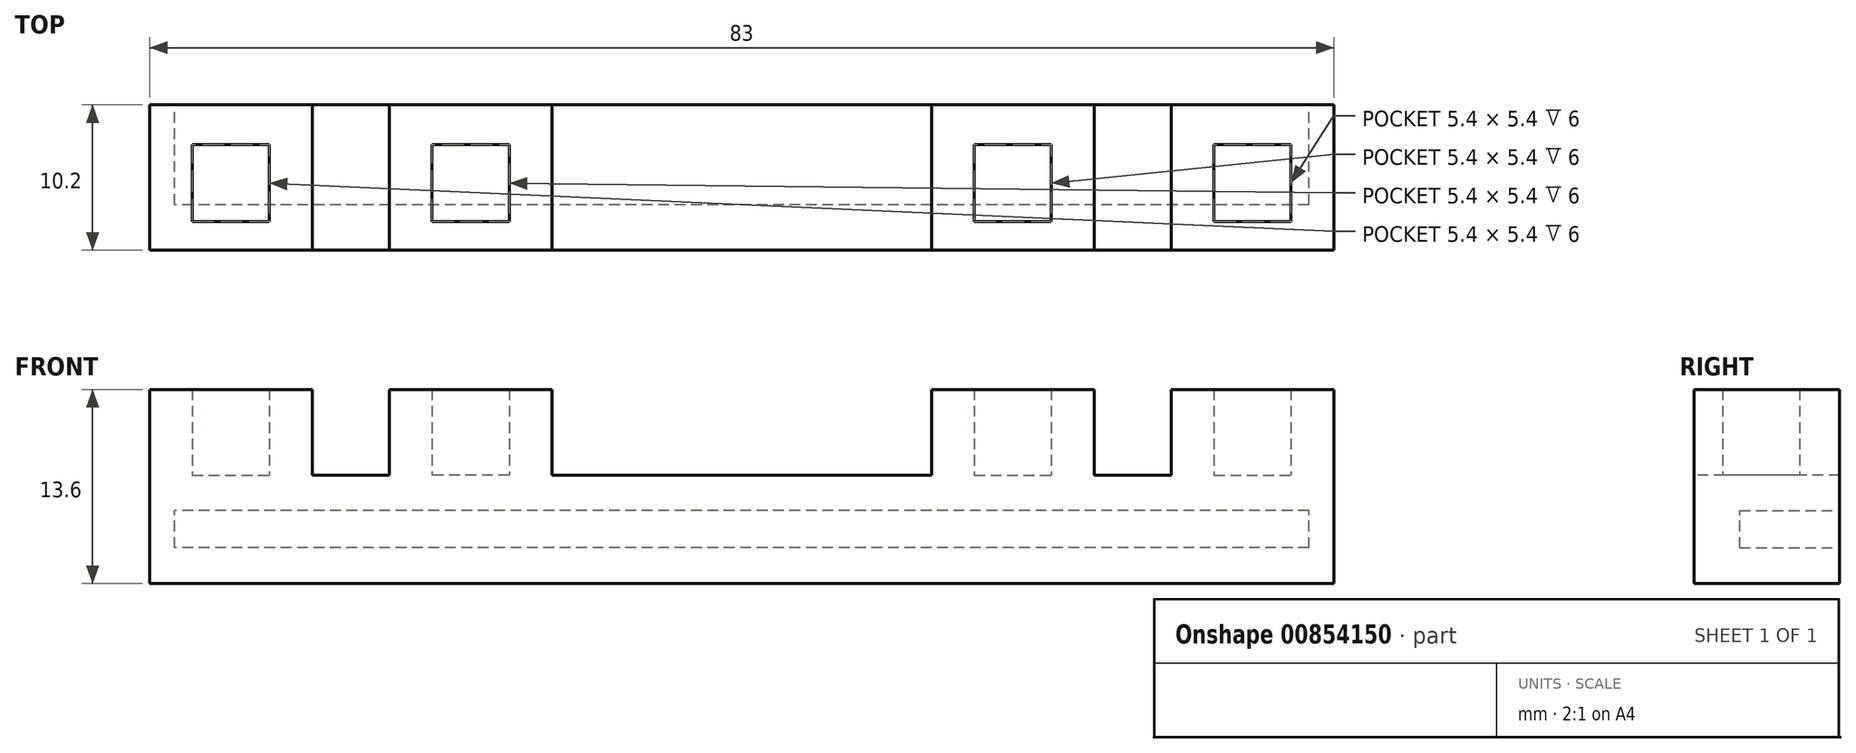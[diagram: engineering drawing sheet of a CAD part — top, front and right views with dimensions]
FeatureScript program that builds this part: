
annotation { "Feature Type Name" : "Feature", "Feature Type Description" : "" }
export const myFeature = defineFeature(function(context is Context, id is Id, definition is map)
    precondition{}
    {
        {
            var Q0;
            Q0=qCreatedBy(makeId("Front.planeOp"),FACE);
            var sketch = newSketch(context, id + "F0", { "sketchPlane" : qUnion([Q0])});
            skLineSegment(sketch, "E0.bottom", {"start": v(41.5, -3.8) * mm, "end": v(-41.5, -3.8) * mm});
            skLineSegment(sketch, "E0.top", {"start": v(41.5, 3.8) * mm, "end": v(-41.5, 3.8) * mm});
            skLineSegment(sketch, "E0.left", {"start": v(41.5, -3.8) * mm, "end": v(41.5, 3.8) * mm});
            skLineSegment(sketch, "E0.right", {"start": v(-41.5, -3.8) * mm, "end": v(-41.5, 3.8) * mm});
            skPoint(sketch, "E0.middle", {"position": v(0, 0) * mm});
            skLineSegment(sketch, "E1.bottom", {"start": v(39.75, -1.3) * mm, "end": v(-39.75, -1.3) * mm});
            skLineSegment(sketch, "E1.top", {"start": v(39.75, 1.3) * mm, "end": v(-39.75, 1.3) * mm});
            skLineSegment(sketch, "E1.left", {"start": v(39.75, -1.3) * mm, "end": v(39.75, 1.3) * mm});
            skLineSegment(sketch, "E1.right", {"start": v(-39.75, -1.3) * mm, "end": v(-39.75, 1.3) * mm});
            skSolve(sketch);
        }
        {
            var Q0;
            Q0=makeQuery(id+"F0.imprint","IMPRINT",FACE,{"disambiguationData":[TD([[makeQuery(id+"F0.imprint","IMPRINT",EDGE,{"derivedFrom":sQuery(id+"F0.wireOp",EDGE,"E0.bottom")}),-1.0]])]});
            extrude(context, id + "F1", {"entities" : qUnion([Q0]), "depth" : 7 * mm, "offsetDistance" : 25 * mm});
        }
        {
            var Q0;
            Q0=makeQuery(id+"F1.opExtrude","CAP_FACE",FACE,{"disambiguationData":[OSD([sQuery(id+"F0.wireOp",EDGE,"E0.bottom"),sQuery(id+"F0.wireOp",EDGE,"E0.top"),sQuery(id+"F0.wireOp",EDGE,"E0.left"),sQuery(id+"F0.wireOp",EDGE,"E0.right"),sQuery(id+"F0.wireOp",EDGE,"E1.bottom"),sQuery(id+"F0.wireOp",EDGE,"E1.top"),sQuery(id+"F0.wireOp",EDGE,"E1.left"),sQuery(id+"F0.wireOp",EDGE,"E1.right")])],"isStart":false});
            var sketch = newSketch(context, id + "F2", { "sketchPlane" : qUnion([Q0])});
            skLineSegment(sketch, "E2.bottom", {"start": v(-41.5, 3.8) * mm, "end": v(41.5, 3.8) * mm});
            skLineSegment(sketch, "E2.top", {"start": v(-41.5, -3.8) * mm, "end": v(41.5, -3.8) * mm});
            skLineSegment(sketch, "E2.left", {"start": v(-41.5, 3.8) * mm, "end": v(-41.5, -3.8) * mm});
            skLineSegment(sketch, "E2.right", {"start": v(41.5, 3.8) * mm, "end": v(41.5, -3.8) * mm});
            skSolve(sketch);
        }
        {
            var Q0;
            Q0=makeQuery(id+"F2.imprint","IMPRINT",FACE,{"disambiguationData":[TD([[makeQuery(id+"F2.imprint","IMPRINT",EDGE,{"derivedFrom":sQuery(id+"F2.wireOp",EDGE,"E2.bottom")}),1.0]])]});
            var Q1;
            Q1=makeQuery(id+"F2.imprint","IMPRINT",FACE,{"disambiguationData":[TD([[makeQuery(id+"F2.imprint","IMPRINT",EDGE,{"derivedFrom":makeQuery(id+"F1.opExtrude","CAP_EDGE",EDGE,{"disambiguationData":[OSD([sQuery(id+"F0.wireOp",EDGE,"E1.bottom")])],"isStart":false})}),-1.0]])]});
            extrude(context, id + "F3", {"entities" : qUnion([Q0, Q1]), "operationType" : NewBodyOperationType.ADD, "depth" : 3.2 * mm, "offsetDistance" : 25 * mm});
        }
        {
            var Q0;
            Q0=makeQuery(id+"F3.boolean.opBoolean","MERGE",FACE,{"derivedFrom":[makeQuery(id+"F1.opExtrude","SWEPT_FACE",FACE,{"disambiguationData":[OSD([sQuery(id+"F0.wireOp",EDGE,"E0.top")])]}),makeQuery(id+"F3.opExtrude","SWEPT_FACE",FACE,{"disambiguationData":[OSD([sQuery(id+"F2.wireOp",EDGE,"E2.bottom")])]})]});
            var sketch = newSketch(context, id + "F4", { "sketchPlane" : qUnion([Q0])});
            skLineSegment(sketch, "E3.bottom", {"start": v(-41.5, -10.2) * mm, "end": v(41.5, -10.2) * mm});
            skLineSegment(sketch, "E3.top", {"start": v(-41.5, 0) * mm, "end": v(41.5, 0) * mm});
            skLineSegment(sketch, "E3.left", {"start": v(-41.5, -10.2) * mm, "end": v(-41.5, 0) * mm});
            skLineSegment(sketch, "E4", {"start": v(0.5, 0) * mm, "end": v(0.5, -10.2) * mm});
            skLineSegment(sketch, "E5", {"start": v(-4.9, 0) * mm, "end": v(-4.9, -10.2) * mm});
            skLineSegment(sketch, "E6", {"start": v(-7.9, 0) * mm, "end": v(-7.9, -10.2) * mm});
            skLineSegment(sketch, "E7", {"start": v(-13.3, 0) * mm, "end": v(-13.3, -10.2) * mm});
            skLineSegment(sketch, "E8", {"start": v(-16.3, 0) * mm, "end": v(-16.3, -10.2) * mm});
            skLineSegment(sketch, "E9", {"start": v(-21.7, 0) * mm, "end": v(-21.7, -10.2) * mm});
            skLineSegment(sketch, "E10", {"start": v(-24.7, 0) * mm, "end": v(-24.7, -10.2) * mm});
            skLineSegment(sketch, "E11", {"start": v(-30.1, 0) * mm, "end": v(-30.1, -10.2) * mm});
            skLineSegment(sketch, "E12", {"start": v(-33.1, 0) * mm, "end": v(-33.1, -10.2) * mm});
            skLineSegment(sketch, "E13", {"start": v(-38.5, 0) * mm, "end": v(-38.5, -10.2) * mm});
            skLineSegment(sketch, "E14", {"start": v(0, 0) * mm, "end": v(0, -13.13) * mm, "construction": true});
            skLineSegment(sketch, "E15.MirrorCS", {"start": v(-0.5, 0) * mm, "end": v(-0.5, -10.2) * mm});
            skLineSegment(sketch, "E16", {"start": v(-41.5, -2.8) * mm, "end": v(41.5, -2.8) * mm});
            skLineSegment(sketch, "E17", {"start": v(41.5, -8.2) * mm, "end": v(-41.5, -8.2) * mm});
            skLineSegment(sketch, "E18.MirrorCS", {"start": v(16.3, 0) * mm, "end": v(16.3, -10.2) * mm});
            skLineSegment(sketch, "E19.MirrorCS", {"start": v(21.7, 0) * mm, "end": v(21.7, -10.2) * mm});
            skLineSegment(sketch, "E20.MirrorCS", {"start": v(24.7, 0) * mm, "end": v(24.7, -10.2) * mm});
            skLineSegment(sketch, "E21.MirrorCS", {"start": v(30.1, 0) * mm, "end": v(30.1, -10.2) * mm});
            skLineSegment(sketch, "E22.MirrorCS", {"start": v(33.1, 0) * mm, "end": v(33.1, -10.2) * mm});
            skLineSegment(sketch, "E23.MirrorCS", {"start": v(38.5, 0) * mm, "end": v(38.5, -10.2) * mm});
            skLineSegment(sketch, "E24.MirrorCS", {"start": v(41.5, -10.2) * mm, "end": v(41.5, 0) * mm});
            skLineSegment(sketch, "E25.MirrorCS", {"start": v(4.9, 0) * mm, "end": v(4.9, -10.2) * mm});
            skLineSegment(sketch, "E26.MirrorCS", {"start": v(13.3, 0) * mm, "end": v(13.3, -10.2) * mm});
            skLineSegment(sketch, "E27.MirrorCS", {"start": v(7.9, 0) * mm, "end": v(7.9, -10.2) * mm});
            skSolve(sketch);
        }
        {
            var Q0;
            {var subQ1=sQuery(id+"F4.wireOp",EDGE,"E3.top");var subQ3=sQuery(id+"F4.wireOp",EDGE,"E13");var subQ4=makeQuery(id+"F4.imprint","INTERSECT",VERTEX,{"derivedFrom":[subQ1,subQ3]});Q0=makeQuery(id+"F4.imprint","IMPRINT",FACE,{"disambiguationData":[TD([[makeQuery(id+"F4.imprint","IMPRINT",EDGE,{"disambiguationData":[TD([[subQ4,-1.0]])],"derivedFrom":subQ3}),-1.0]])]});}
            var Q1;
            {var subQ0=sQuery(id+"F4.wireOp",EDGE,"E12");var subQ1=sQuery(id+"F4.wireOp",EDGE,"E3.top");var subQ2=makeQuery(id+"F4.imprint","INTERSECT",VERTEX,{"derivedFrom":[subQ1,subQ0]});Q1=makeQuery(id+"F4.imprint","IMPRINT",FACE,{"disambiguationData":[TD([[makeQuery(id+"F4.imprint","IMPRINT",EDGE,{"disambiguationData":[TD([[subQ2,1.0]])],"derivedFrom":subQ1}),-1.0]])]});}
            var Q2;
            {var subQ0=sQuery(id+"F4.wireOp",EDGE,"E11");var subQ1=sQuery(id+"F4.wireOp",EDGE,"E3.top");var subQ2=makeQuery(id+"F4.imprint","INTERSECT",VERTEX,{"derivedFrom":[subQ1,subQ0]});Q2=makeQuery(id+"F4.imprint","IMPRINT",FACE,{"disambiguationData":[TD([[makeQuery(id+"F4.imprint","IMPRINT",EDGE,{"disambiguationData":[TD([[subQ2,1.0]])],"derivedFrom":subQ1}),-1.0]])]});}
            var Q3;
            {var subQ0=sQuery(id+"F4.wireOp",EDGE,"E9");var subQ1=sQuery(id+"F4.wireOp",EDGE,"E3.top");var subQ2=makeQuery(id+"F4.imprint","INTERSECT",VERTEX,{"derivedFrom":[subQ1,subQ0]});Q3=makeQuery(id+"F4.imprint","IMPRINT",FACE,{"disambiguationData":[TD([[makeQuery(id+"F4.imprint","IMPRINT",EDGE,{"disambiguationData":[TD([[subQ2,1.0]])],"derivedFrom":subQ1}),-1.0]])]});}
            var Q4;
            {var subQ0=sQuery(id+"F4.wireOp",EDGE,"E8");var subQ1=sQuery(id+"F4.wireOp",EDGE,"E3.top");var subQ2=makeQuery(id+"F4.imprint","INTERSECT",VERTEX,{"derivedFrom":[subQ1,subQ0]});Q4=makeQuery(id+"F4.imprint","IMPRINT",FACE,{"disambiguationData":[TD([[makeQuery(id+"F4.imprint","IMPRINT",EDGE,{"disambiguationData":[TD([[subQ2,1.0]])],"derivedFrom":subQ1}),-1.0]])]});}
            var Q5;
            {var subQ0=sQuery(id+"F4.wireOp",EDGE,"E7");var subQ1=sQuery(id+"F4.wireOp",EDGE,"E3.top");var subQ2=makeQuery(id+"F4.imprint","INTERSECT",VERTEX,{"derivedFrom":[subQ1,subQ0]});Q5=makeQuery(id+"F4.imprint","IMPRINT",FACE,{"disambiguationData":[TD([[makeQuery(id+"F4.imprint","IMPRINT",EDGE,{"disambiguationData":[TD([[subQ2,1.0]])],"derivedFrom":subQ1}),-1.0]])]});}
            var Q6;
            {var subQ0=sQuery(id+"F4.wireOp",EDGE,"E18.MirrorCS");var subQ1=sQuery(id+"F4.wireOp",EDGE,"E3.top");var subQ2=makeQuery(id+"F4.imprint","INTERSECT",VERTEX,{"derivedFrom":[subQ1,subQ0]});Q6=makeQuery(id+"F4.imprint","IMPRINT",FACE,{"disambiguationData":[TD([[makeQuery(id+"F4.imprint","IMPRINT",EDGE,{"disambiguationData":[TD([[subQ2,1.0]])],"derivedFrom":subQ1}),-1.0]])]});}
            var Q7;
            {var subQ0=sQuery(id+"F4.wireOp",EDGE,"E18.MirrorCS");var subQ1=sQuery(id+"F4.wireOp",EDGE,"E3.top");var subQ2=makeQuery(id+"F4.imprint","INTERSECT",VERTEX,{"derivedFrom":[subQ1,subQ0]});Q7=makeQuery(id+"F4.imprint","IMPRINT",FACE,{"disambiguationData":[TD([[makeQuery(id+"F4.imprint","IMPRINT",EDGE,{"disambiguationData":[TD([[subQ2,-1.0]])],"derivedFrom":subQ1}),-1.0]])]});}
            var Q8;
            {var subQ0=sQuery(id+"F4.wireOp",EDGE,"E19.MirrorCS");var subQ1=sQuery(id+"F4.wireOp",EDGE,"E3.top");var subQ2=makeQuery(id+"F4.imprint","INTERSECT",VERTEX,{"derivedFrom":[subQ1,subQ0]});Q8=makeQuery(id+"F4.imprint","IMPRINT",FACE,{"disambiguationData":[TD([[makeQuery(id+"F4.imprint","IMPRINT",EDGE,{"disambiguationData":[TD([[subQ2,-1.0]])],"derivedFrom":subQ1}),-1.0]])]});}
            var Q9;
            {var subQ0=sQuery(id+"F4.wireOp",EDGE,"E21.MirrorCS");var subQ1=sQuery(id+"F4.wireOp",EDGE,"E3.top");var subQ2=makeQuery(id+"F4.imprint","INTERSECT",VERTEX,{"derivedFrom":[subQ1,subQ0]});Q9=makeQuery(id+"F4.imprint","IMPRINT",FACE,{"disambiguationData":[TD([[makeQuery(id+"F4.imprint","IMPRINT",EDGE,{"disambiguationData":[TD([[subQ2,-1.0]])],"derivedFrom":subQ1}),-1.0]])]});}
            var Q10;
            {var subQ0=sQuery(id+"F4.wireOp",EDGE,"E22.MirrorCS");var subQ1=sQuery(id+"F4.wireOp",EDGE,"E3.top");var subQ2=makeQuery(id+"F4.imprint","INTERSECT",VERTEX,{"derivedFrom":[subQ1,subQ0]});Q10=makeQuery(id+"F4.imprint","IMPRINT",FACE,{"disambiguationData":[TD([[makeQuery(id+"F4.imprint","IMPRINT",EDGE,{"disambiguationData":[TD([[subQ2,-1.0]])],"derivedFrom":subQ1}),-1.0]])]});}
            var Q11;
            {var subQ0=sQuery(id+"F4.wireOp",EDGE,"E24.MirrorCS");var subQ5=sQuery(id+"F4.wireOp",EDGE,"E16");var subQ6=makeQuery(id+"F4.imprint","INTERSECT",VERTEX,{"derivedFrom":[subQ5,subQ0]});Q11=makeQuery(id+"F4.imprint","IMPRINT",FACE,{"disambiguationData":[TD([[makeQuery(id+"F4.imprint","IMPRINT",EDGE,{"disambiguationData":[TD([[subQ6,1.0]])],"derivedFrom":subQ5}),1.0]])]});}
            var Q12;
            {var subQ0=sQuery(id+"F4.wireOp",EDGE,"E16");var subQ1=sQuery(id+"F4.wireOp",EDGE,"E3.left");var subQ2=makeQuery(id+"F4.imprint","INTERSECT",VERTEX,{"derivedFrom":[subQ1,subQ0]});Q12=makeQuery(id+"F4.imprint","IMPRINT",FACE,{"disambiguationData":[TD([[makeQuery(id+"F4.imprint","IMPRINT",EDGE,{"disambiguationData":[TD([[subQ2,1.0]])],"derivedFrom":subQ1}),-1.0]])]});}
            var Q13;
            {var subQ0=sQuery(id+"F4.wireOp",EDGE,"E3.left");var subQ1=sQuery(id+"F4.wireOp",EDGE,"E3.bottom");var subQ2=makeQuery(id+"F4.imprint","INTERSECT",VERTEX,{"derivedFrom":[subQ1,subQ0]});Q13=makeQuery(id+"F4.imprint","IMPRINT",FACE,{"disambiguationData":[TD([[makeQuery(id+"F4.imprint","IMPRINT",EDGE,{"disambiguationData":[TD([[subQ2,1.0]])],"derivedFrom":subQ1}),-1.0]])]});}
            var Q14;
            {var subQ0=sQuery(id+"F4.wireOp",EDGE,"E12");var subQ1=sQuery(id+"F4.wireOp",EDGE,"E3.bottom");var subQ2=makeQuery(id+"F4.imprint","INTERSECT",VERTEX,{"derivedFrom":[subQ1,subQ0]});Q14=makeQuery(id+"F4.imprint","IMPRINT",FACE,{"disambiguationData":[TD([[makeQuery(id+"F4.imprint","IMPRINT",EDGE,{"disambiguationData":[TD([[subQ2,-1.0]])],"derivedFrom":subQ1}),-1.0]])]});}
            var Q15;
            {var subQ0=sQuery(id+"F4.wireOp",EDGE,"E11");var subQ1=sQuery(id+"F4.wireOp",EDGE,"E3.bottom");var subQ2=makeQuery(id+"F4.imprint","INTERSECT",VERTEX,{"derivedFrom":[subQ1,subQ0]});Q15=makeQuery(id+"F4.imprint","IMPRINT",FACE,{"disambiguationData":[TD([[makeQuery(id+"F4.imprint","IMPRINT",EDGE,{"disambiguationData":[TD([[subQ2,-1.0]])],"derivedFrom":subQ1}),-1.0]])]});}
            var Q16;
            {var subQ0=sQuery(id+"F4.wireOp",EDGE,"E16");var subQ1=sQuery(id+"F4.wireOp",EDGE,"E11");var subQ2=makeQuery(id+"F4.imprint","INTERSECT",VERTEX,{"derivedFrom":[subQ1,subQ0]});Q16=makeQuery(id+"F4.imprint","IMPRINT",FACE,{"disambiguationData":[TD([[makeQuery(id+"F4.imprint","IMPRINT",EDGE,{"disambiguationData":[TD([[subQ2,-1.0]])],"derivedFrom":subQ1}),-1.0]])]});}
            var Q17;
            {var subQ0=sQuery(id+"F4.wireOp",EDGE,"E9");var subQ1=sQuery(id+"F4.wireOp",EDGE,"E3.bottom");var subQ2=makeQuery(id+"F4.imprint","INTERSECT",VERTEX,{"derivedFrom":[subQ1,subQ0]});Q17=makeQuery(id+"F4.imprint","IMPRINT",FACE,{"disambiguationData":[TD([[makeQuery(id+"F4.imprint","IMPRINT",EDGE,{"disambiguationData":[TD([[subQ2,-1.0]])],"derivedFrom":subQ1}),-1.0]])]});}
            var Q18;
            {var subQ0=sQuery(id+"F4.wireOp",EDGE,"E8");var subQ1=sQuery(id+"F4.wireOp",EDGE,"E3.bottom");var subQ2=makeQuery(id+"F4.imprint","INTERSECT",VERTEX,{"derivedFrom":[subQ1,subQ0]});Q18=makeQuery(id+"F4.imprint","IMPRINT",FACE,{"disambiguationData":[TD([[makeQuery(id+"F4.imprint","IMPRINT",EDGE,{"disambiguationData":[TD([[subQ2,-1.0]])],"derivedFrom":subQ1}),-1.0]])]});}
            var Q19;
            {var subQ0=sQuery(id+"F4.wireOp",EDGE,"E16");var subQ1=sQuery(id+"F4.wireOp",EDGE,"E9");var subQ2=makeQuery(id+"F4.imprint","INTERSECT",VERTEX,{"derivedFrom":[subQ1,subQ0]});Q19=makeQuery(id+"F4.imprint","IMPRINT",FACE,{"disambiguationData":[TD([[makeQuery(id+"F4.imprint","IMPRINT",EDGE,{"disambiguationData":[TD([[subQ2,-1.0]])],"derivedFrom":subQ1}),-1.0]])]});}
            var Q20;
            {var subQ0=sQuery(id+"F4.wireOp",EDGE,"E16");var subQ1=sQuery(id+"F4.wireOp",EDGE,"E7");var subQ2=makeQuery(id+"F4.imprint","INTERSECT",VERTEX,{"derivedFrom":[subQ1,subQ0]});Q20=makeQuery(id+"F4.imprint","IMPRINT",FACE,{"disambiguationData":[TD([[makeQuery(id+"F4.imprint","IMPRINT",EDGE,{"disambiguationData":[TD([[subQ2,-1.0]])],"derivedFrom":subQ1}),-1.0]])]});}
            var Q21;
            {var subQ0=sQuery(id+"F4.wireOp",EDGE,"E7");var subQ1=sQuery(id+"F4.wireOp",EDGE,"E3.bottom");var subQ2=makeQuery(id+"F4.imprint","INTERSECT",VERTEX,{"derivedFrom":[subQ1,subQ0]});Q21=makeQuery(id+"F4.imprint","IMPRINT",FACE,{"disambiguationData":[TD([[makeQuery(id+"F4.imprint","IMPRINT",EDGE,{"disambiguationData":[TD([[subQ2,-1.0]])],"derivedFrom":subQ1}),-1.0]])]});}
            var Q22;
            {var subQ0=sQuery(id+"F4.wireOp",EDGE,"E24.MirrorCS");var subQ1=sQuery(id+"F4.wireOp",EDGE,"E3.bottom");var subQ2=makeQuery(id+"F4.imprint","INTERSECT",VERTEX,{"derivedFrom":[subQ1,subQ0]});Q22=makeQuery(id+"F4.imprint","IMPRINT",FACE,{"disambiguationData":[TD([[makeQuery(id+"F4.imprint","IMPRINT",EDGE,{"disambiguationData":[TD([[subQ2,-1.0]])],"derivedFrom":subQ1}),-1.0]])]});}
            var Q23;
            {var subQ0=sQuery(id+"F4.wireOp",EDGE,"E22.MirrorCS");var subQ1=sQuery(id+"F4.wireOp",EDGE,"E3.bottom");var subQ2=makeQuery(id+"F4.imprint","INTERSECT",VERTEX,{"derivedFrom":[subQ1,subQ0]});Q23=makeQuery(id+"F4.imprint","IMPRINT",FACE,{"disambiguationData":[TD([[makeQuery(id+"F4.imprint","IMPRINT",EDGE,{"disambiguationData":[TD([[subQ2,1.0]])],"derivedFrom":subQ1}),-1.0]])]});}
            var Q24;
            {var subQ0=sQuery(id+"F4.wireOp",EDGE,"E21.MirrorCS");var subQ1=sQuery(id+"F4.wireOp",EDGE,"E3.bottom");var subQ2=makeQuery(id+"F4.imprint","INTERSECT",VERTEX,{"derivedFrom":[subQ1,subQ0]});Q24=makeQuery(id+"F4.imprint","IMPRINT",FACE,{"disambiguationData":[TD([[makeQuery(id+"F4.imprint","IMPRINT",EDGE,{"disambiguationData":[TD([[subQ2,1.0]])],"derivedFrom":subQ1}),-1.0]])]});}
            var Q25;
            {var subQ0=sQuery(id+"F4.wireOp",EDGE,"E19.MirrorCS");var subQ1=sQuery(id+"F4.wireOp",EDGE,"E3.bottom");var subQ2=makeQuery(id+"F4.imprint","INTERSECT",VERTEX,{"derivedFrom":[subQ1,subQ0]});Q25=makeQuery(id+"F4.imprint","IMPRINT",FACE,{"disambiguationData":[TD([[makeQuery(id+"F4.imprint","IMPRINT",EDGE,{"disambiguationData":[TD([[subQ2,1.0]])],"derivedFrom":subQ1}),-1.0]])]});}
            var Q26;
            {var subQ0=sQuery(id+"F4.wireOp",EDGE,"E18.MirrorCS");var subQ1=sQuery(id+"F4.wireOp",EDGE,"E3.bottom");var subQ2=makeQuery(id+"F4.imprint","INTERSECT",VERTEX,{"derivedFrom":[subQ1,subQ0]});Q26=makeQuery(id+"F4.imprint","IMPRINT",FACE,{"disambiguationData":[TD([[makeQuery(id+"F4.imprint","IMPRINT",EDGE,{"disambiguationData":[TD([[subQ2,1.0]])],"derivedFrom":subQ1}),-1.0]])]});}
            var Q27;
            {var subQ0=sQuery(id+"F4.wireOp",EDGE,"E18.MirrorCS");var subQ1=sQuery(id+"F4.wireOp",EDGE,"E3.bottom");var subQ2=makeQuery(id+"F4.imprint","INTERSECT",VERTEX,{"derivedFrom":[subQ1,subQ0]});Q27=makeQuery(id+"F4.imprint","IMPRINT",FACE,{"disambiguationData":[TD([[makeQuery(id+"F4.imprint","IMPRINT",EDGE,{"disambiguationData":[TD([[subQ2,-1.0]])],"derivedFrom":subQ1}),-1.0]])]});}
            var Q28;
            {var subQ0=sQuery(id+"F4.wireOp",EDGE,"E26.MirrorCS");var subQ1=sQuery(id+"F4.wireOp",EDGE,"E16");var subQ2=makeQuery(id+"F4.imprint","INTERSECT",VERTEX,{"derivedFrom":[subQ1,subQ0]});Q28=makeQuery(id+"F4.imprint","IMPRINT",FACE,{"disambiguationData":[TD([[makeQuery(id+"F4.imprint","IMPRINT",EDGE,{"disambiguationData":[TD([[subQ2,-1.0]])],"derivedFrom":subQ1}),-1.0]])]});}
            var Q29;
            {var subQ0=sQuery(id+"F4.wireOp",EDGE,"E19.MirrorCS");var subQ1=sQuery(id+"F4.wireOp",EDGE,"E16");var subQ2=makeQuery(id+"F4.imprint","INTERSECT",VERTEX,{"derivedFrom":[subQ1,subQ0]});Q29=makeQuery(id+"F4.imprint","IMPRINT",FACE,{"disambiguationData":[TD([[makeQuery(id+"F4.imprint","IMPRINT",EDGE,{"disambiguationData":[TD([[subQ2,-1.0]])],"derivedFrom":subQ1}),-1.0]])]});}
            var Q30;
            {var subQ0=sQuery(id+"F4.wireOp",EDGE,"E21.MirrorCS");var subQ1=sQuery(id+"F4.wireOp",EDGE,"E16");var subQ2=makeQuery(id+"F4.imprint","INTERSECT",VERTEX,{"derivedFrom":[subQ1,subQ0]});Q30=makeQuery(id+"F4.imprint","IMPRINT",FACE,{"disambiguationData":[TD([[makeQuery(id+"F4.imprint","IMPRINT",EDGE,{"disambiguationData":[TD([[subQ2,-1.0]])],"derivedFrom":subQ1}),-1.0]])]});}
            var Q31;
            {var subQ0=sQuery(id+"F4.wireOp",EDGE,"E24.MirrorCS");var subQ1=sQuery(id+"F4.wireOp",EDGE,"E16");var subQ2=makeQuery(id+"F4.imprint","INTERSECT",VERTEX,{"derivedFrom":[subQ1,subQ0]});Q31=makeQuery(id+"F4.imprint","IMPRINT",FACE,{"disambiguationData":[TD([[makeQuery(id+"F4.imprint","IMPRINT",EDGE,{"disambiguationData":[TD([[subQ2,1.0]])],"derivedFrom":subQ1}),-1.0]])]});}
            var Q32;
            {var subQ0=sQuery(id+"F4.wireOp",EDGE,"E12");var subQ1=sQuery(id+"F4.wireOp",EDGE,"E3.top");var subQ2=makeQuery(id+"F4.imprint","INTERSECT",VERTEX,{"derivedFrom":[subQ1,subQ0]});Q32=makeQuery(id+"F4.imprint","IMPRINT",FACE,{"disambiguationData":[TD([[makeQuery(id+"F4.imprint","IMPRINT",EDGE,{"disambiguationData":[TD([[subQ2,-1.0]])],"derivedFrom":subQ1}),1.0]])]});}
            var Q33;
            {var subQ0=sQuery(id+"F4.wireOp",EDGE,"E11");var subQ1=sQuery(id+"F4.wireOp",EDGE,"E3.top");var subQ2=makeQuery(id+"F4.imprint","INTERSECT",VERTEX,{"derivedFrom":[subQ1,subQ0]});Q33=makeQuery(id+"F4.imprint","IMPRINT",FACE,{"disambiguationData":[TD([[makeQuery(id+"F4.imprint","IMPRINT",EDGE,{"disambiguationData":[TD([[subQ2,-1.0]])],"derivedFrom":subQ1}),1.0]])]});}
            var Q34;
            {var subQ0=sQuery(id+"F4.wireOp",EDGE,"E9");var subQ1=sQuery(id+"F4.wireOp",EDGE,"E3.top");var subQ2=makeQuery(id+"F4.imprint","INTERSECT",VERTEX,{"derivedFrom":[subQ1,subQ0]});Q34=makeQuery(id+"F4.imprint","IMPRINT",FACE,{"disambiguationData":[TD([[makeQuery(id+"F4.imprint","IMPRINT",EDGE,{"disambiguationData":[TD([[subQ2,-1.0]])],"derivedFrom":subQ1}),1.0]])]});}
            var Q35;
            {var subQ0=sQuery(id+"F4.wireOp",EDGE,"E8");var subQ1=sQuery(id+"F4.wireOp",EDGE,"E3.top");var subQ2=makeQuery(id+"F4.imprint","INTERSECT",VERTEX,{"derivedFrom":[subQ1,subQ0]});Q35=makeQuery(id+"F4.imprint","IMPRINT",FACE,{"disambiguationData":[TD([[makeQuery(id+"F4.imprint","IMPRINT",EDGE,{"disambiguationData":[TD([[subQ2,-1.0]])],"derivedFrom":subQ1}),1.0]])]});}
            var Q36;
            {var subQ0=sQuery(id+"F4.wireOp",EDGE,"E7");var subQ1=sQuery(id+"F4.wireOp",EDGE,"E3.top");var subQ2=makeQuery(id+"F4.imprint","INTERSECT",VERTEX,{"derivedFrom":[subQ1,subQ0]});Q36=makeQuery(id+"F4.imprint","IMPRINT",FACE,{"disambiguationData":[TD([[makeQuery(id+"F4.imprint","IMPRINT",EDGE,{"disambiguationData":[TD([[subQ2,-1.0]])],"derivedFrom":subQ1}),1.0]])]});}
            var Q37;
            {var subQ0=sQuery(id+"F4.wireOp",EDGE,"E18.MirrorCS");var subQ1=sQuery(id+"F4.wireOp",EDGE,"E3.top");var subQ2=makeQuery(id+"F4.imprint","INTERSECT",VERTEX,{"derivedFrom":[subQ1,subQ0]});Q37=makeQuery(id+"F4.imprint","IMPRINT",FACE,{"disambiguationData":[TD([[makeQuery(id+"F4.imprint","IMPRINT",EDGE,{"disambiguationData":[TD([[subQ2,-1.0]])],"derivedFrom":subQ1}),1.0]])]});}
            var Q38;
            {var subQ0=sQuery(id+"F4.wireOp",EDGE,"E18.MirrorCS");var subQ1=sQuery(id+"F4.wireOp",EDGE,"E3.top");var subQ2=makeQuery(id+"F4.imprint","INTERSECT",VERTEX,{"derivedFrom":[subQ1,subQ0]});Q38=makeQuery(id+"F4.imprint","IMPRINT",FACE,{"disambiguationData":[TD([[makeQuery(id+"F4.imprint","IMPRINT",EDGE,{"disambiguationData":[TD([[subQ2,1.0]])],"derivedFrom":subQ1}),1.0]])]});}
            var Q39;
            {var subQ0=sQuery(id+"F4.wireOp",EDGE,"E19.MirrorCS");var subQ1=sQuery(id+"F4.wireOp",EDGE,"E3.top");var subQ2=makeQuery(id+"F4.imprint","INTERSECT",VERTEX,{"derivedFrom":[subQ1,subQ0]});Q39=makeQuery(id+"F4.imprint","IMPRINT",FACE,{"disambiguationData":[TD([[makeQuery(id+"F4.imprint","IMPRINT",EDGE,{"disambiguationData":[TD([[subQ2,1.0]])],"derivedFrom":subQ1}),1.0]])]});}
            var Q40;
            {var subQ0=sQuery(id+"F4.wireOp",EDGE,"E22.MirrorCS");var subQ1=sQuery(id+"F4.wireOp",EDGE,"E3.top");var subQ2=makeQuery(id+"F4.imprint","INTERSECT",VERTEX,{"derivedFrom":[subQ1,subQ0]});Q40=makeQuery(id+"F4.imprint","IMPRINT",FACE,{"disambiguationData":[TD([[makeQuery(id+"F4.imprint","IMPRINT",EDGE,{"disambiguationData":[TD([[subQ2,1.0]])],"derivedFrom":subQ1}),1.0]])]});}
            var Q41;
            {var subQ0=sQuery(id+"F4.wireOp",EDGE,"E21.MirrorCS");var subQ1=sQuery(id+"F4.wireOp",EDGE,"E3.top");var subQ2=makeQuery(id+"F4.imprint","INTERSECT",VERTEX,{"derivedFrom":[subQ1,subQ0]});Q41=makeQuery(id+"F4.imprint","IMPRINT",FACE,{"disambiguationData":[TD([[makeQuery(id+"F4.imprint","IMPRINT",EDGE,{"disambiguationData":[TD([[subQ2,1.0]])],"derivedFrom":subQ1}),1.0]])]});}
            extrude(context, id + "F5", {"entities" : qUnion([Q0, Q1, Q2, Q3, Q4, Q5, Q6, Q7, Q8, Q9, Q10, Q11, Q12, Q13, Q14, Q15, Q16, Q17, Q18, Q19, Q20, Q21, Q22, Q23, Q24, Q25, Q26, Q27, Q28, Q29, Q30, Q31, Q32, Q33, Q34, Q35, Q36, Q37, Q38, Q39, Q40, Q41]), "operationType" : NewBodyOperationType.ADD, "depth" : 6 * mm, "offsetDistance" : 25 * mm});
        }
    });
